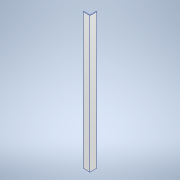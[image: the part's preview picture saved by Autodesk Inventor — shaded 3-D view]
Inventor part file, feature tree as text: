
AUTODESK INVENTOR PART (.ipt)
format: ipt  version: 2022 (Build 260153000, 153)  size: 99,328 bytes
history: native  units: mm
features: extrude x1, sketch x1
ambient origin geometry x8: Origin, YZ Plane, XZ Plane, XY Plane, X Axis, Y Axis, Z Axis, Center Point
bodies: Solid1 (feature_tree)
feature tree (2):
  extrude  "Extrusion1"  Depth=50.0mm
  sketch  "Sketch1"  dims[d0=50.0mm d1=50.0mm d2=5.0mm d3=5.0mm d4=1000.0mm d5=0.0mm]
